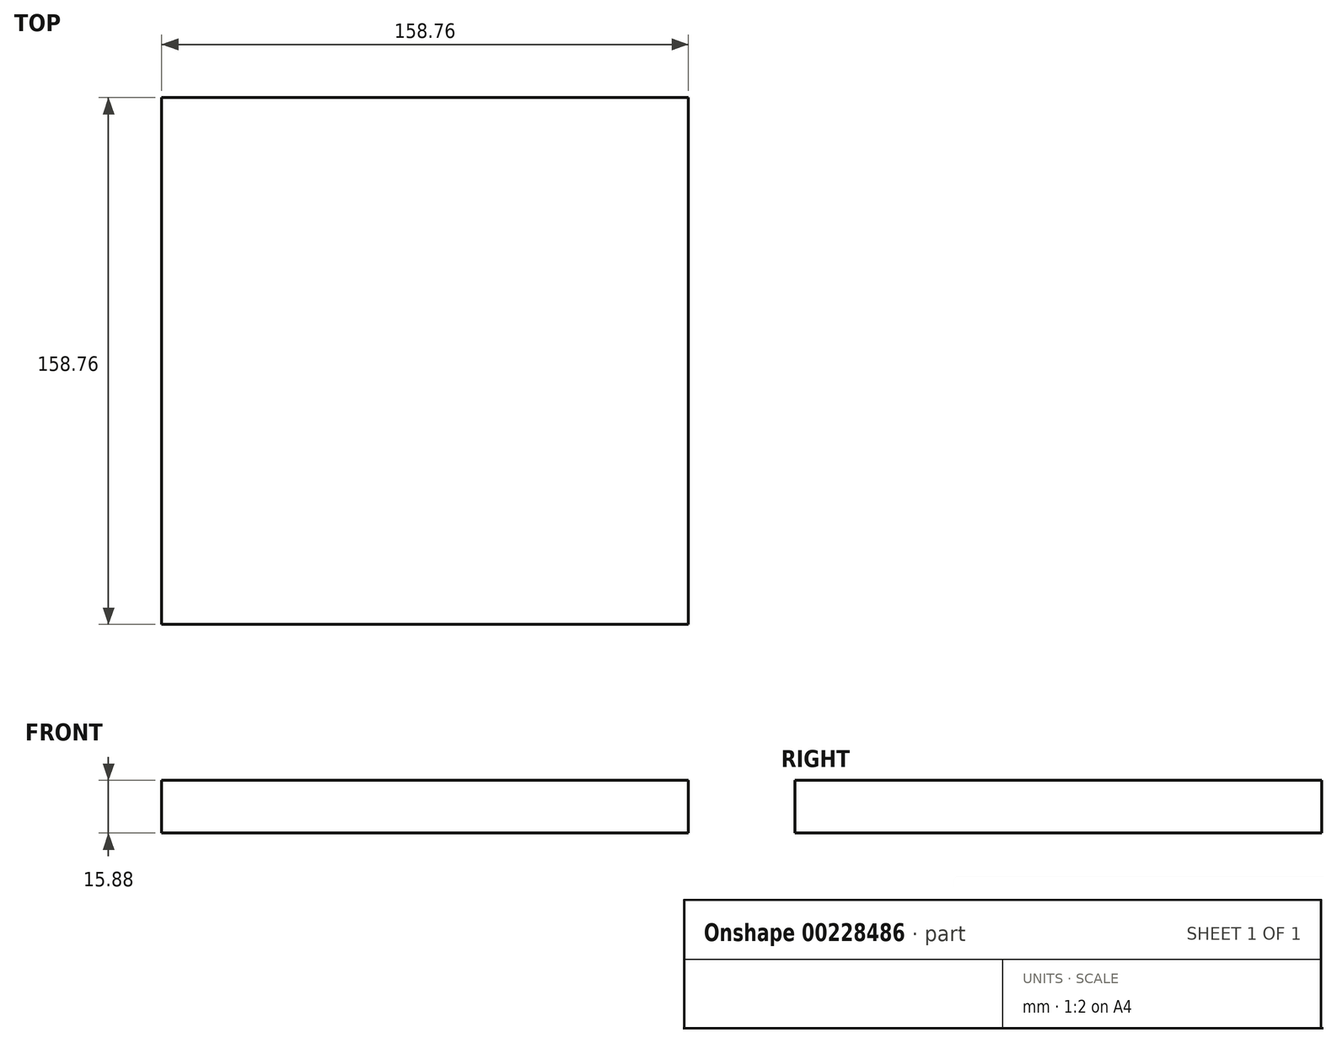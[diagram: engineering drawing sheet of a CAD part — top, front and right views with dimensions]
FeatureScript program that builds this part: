
annotation { "Feature Type Name" : "Feature", "Feature Type Description" : "" }
export const myFeature = defineFeature(function(context is Context, id is Id, definition is map)
    precondition{}
    {
        {
            var Q0;
            Q0=qCreatedBy(makeId("Top.planeOp"),FACE);
            var sketch = newSketch(context, id + "F0", { "sketchPlane" : qUnion([Q0])});
            skLineSegment(sketch, "E0.bottom", {"start": v(79.37, 79.38) * mm, "end": v(-79.38, 79.38) * mm});
            skLineSegment(sketch, "E0.top", {"start": v(79.38, -79.38) * mm, "end": v(-79.38, -79.38) * mm});
            skLineSegment(sketch, "E0.left", {"start": v(79.37, 79.38) * mm, "end": v(79.38, -79.38) * mm});
            skLineSegment(sketch, "E0.right", {"start": v(-79.38, 79.38) * mm, "end": v(-79.38, -79.38) * mm});
            skPoint(sketch, "E0.middle", {"position": v(0, 0) * mm});
            skSolve(sketch);
        }
        {
            var Q0;
            Q0 = qSketchRegion(id + "F0", true);
            extrude(context, id + "F1", {"entities" : qUnion([Q0]), "oppositeDirection" : true, "depth" : 15.88 * mm});
        }
        {
            var Q0;
            Q0=makeQuery(id+"F1.opExtrude","CAP_FACE",FACE,{"disambiguationData":[OSD([sQuery(id+"F0.wireOp",EDGE,"E0.bottom"),sQuery(id+"F0.wireOp",EDGE,"E0.top"),sQuery(id+"F0.wireOp",EDGE,"E0.left"),sQuery(id+"F0.wireOp",EDGE,"E0.right")])],"isStart":true});
            var sketch = newSketch(context, id + "F2", { "sketchPlane" : qUnion([Q0])});
            skLineSegment(sketch, "E1.bottom", {"start": v(-71.44, 71.44) * mm, "end": v(71.44, 71.44) * mm});
            skLineSegment(sketch, "E1.top", {"start": v(-71.44, -71.44) * mm, "end": v(71.44, -71.44) * mm});
            skLineSegment(sketch, "E1.left", {"start": v(-71.44, 71.44) * mm, "end": v(-71.44, -71.44) * mm});
            skLineSegment(sketch, "E1.right", {"start": v(71.44, 71.44) * mm, "end": v(71.44, -71.44) * mm});
            skPoint(sketch, "E1.middle", {"position": v(0, 0) * mm});
            skSolve(sketch);
        }
        {
            var Q0;
            Q0=makeQuery(id+"F2.imprint","IMPRINT",FACE,{"disambiguationData":[TD([[makeQuery(id+"F2.imprint","IMPRINT",EDGE,{"derivedFrom":sQuery(id+"F2.wireOp",EDGE,"E1.bottom")}),-1.0]])]});
            extrude(context, id + "F3", {"entities" : qUnion([Q0]), "operationType" : NewBodyOperationType.ADD, "oppositeDirection" : true, "depth" : 3.56 * mm});
        }
    });
